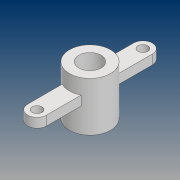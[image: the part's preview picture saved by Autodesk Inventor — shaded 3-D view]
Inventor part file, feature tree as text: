
AUTODESK INVENTOR PART (.ipt)
format: ipt  version: 2021 (Build 250183000, 183)  size: 184,832 bytes
history: native  units: mm
features: extrude x6, sketch x5, fillet x2, hole x1, chamfer x1, projected_geometry x1
ambient origin geometry x8: Origin, YZ Plane, XZ Plane, XY Plane, X Axis, Y Axis, Z Axis, Center Point
bodies: Solid1 (feature_tree)
feature tree (16):
  sketch  "Sketch1"  dims[d0=56.0mm d1=5.0mm]
  extrude  "Extrusion1"  Depth=5.0mm
  extrude  "Extrusion2"  Depth=5.0mm
  extrude  "Extrusion3"  Depth=5.0mm TaperAngle=0.0deg
  hole  "Hole1"  [1 undecoded]
  extrude  "Extrusion4"  Depth=28.0mm TaperAngle=0.0deg
  extrude  "Extrusion5"  Depth=10.0mm TaperAngle=0.0deg
  extrude  "Extrusion6"  Depth=1.0mm
  fillet  "Fillet1"  Radius=3.0mm
  fillet  "Fillet2"  Radius=1.0mm
  chamfer  "Chamfer1"  Distance=1.0mm
  sketch  "Sketch2"  dims[d2=11.8mm d3=5.0mm]
  projected_geometry  "Projected Loop1"
  sketch  "Sketch3"  dims[d4=5.0mm d5=0.0mm d6=18.25mm d7=0.0mm]
  sketch  "Sketch4"  dims[d8=8.0mm d9=0.0mm d10=7.0mm]
  sketch  "Sketch5"  dims[d11=5.2mm d12=6.0mm d13=4.0mm d14=2.0mm d15=90.0deg d16=8.0mm d17=20.594885mm d19=28.0mm d20=0.0mm d21=10.0mm d22=0.0mm d23=6.5mm d24=3.0mm d25=0.0mm d26=1.0mm d27=1.0mm d28=0.5mm d29=2.0mm d30=45.0deg]
note: 1 required parameter value undecoded (feature->parameter linkage not recoverable at this tier; creation-order binding heuristic only, values carry confidence <= 0.55)
